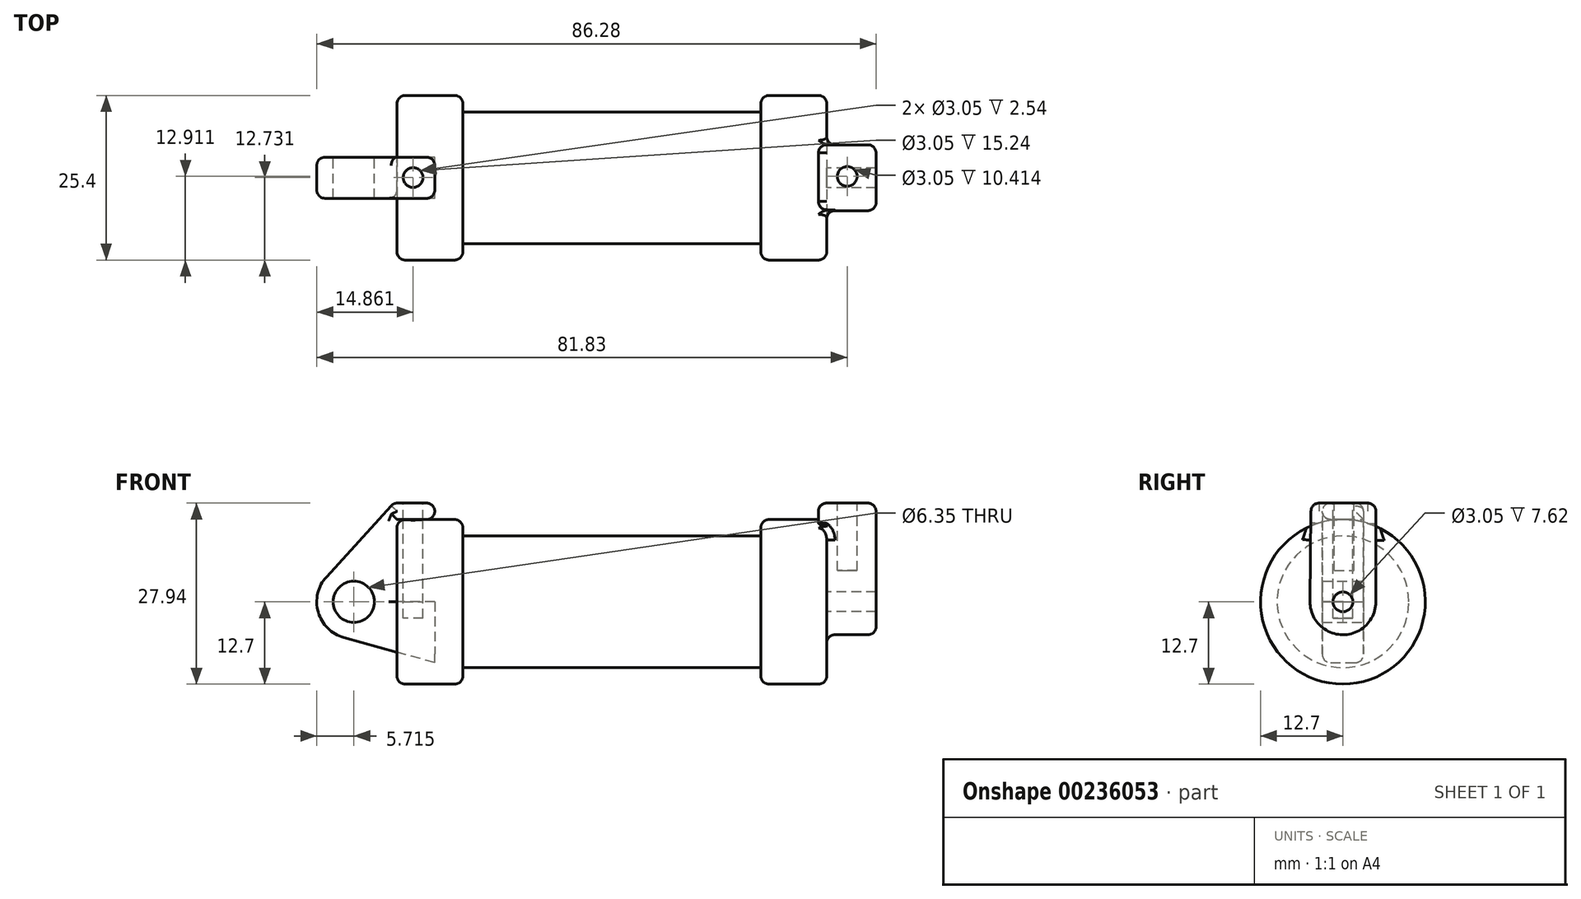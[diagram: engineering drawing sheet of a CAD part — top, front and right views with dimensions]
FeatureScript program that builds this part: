
annotation { "Feature Type Name" : "Feature", "Feature Type Description" : "" }
export const myFeature = defineFeature(function(context is Context, id is Id, definition is map)
    precondition{}
    {
        {
            var Q0;
            Q0=qCreatedBy(makeId("Front.planeOp"),FACE);
            var sketch = newSketch(context, id + "F0", { "sketchPlane" : qUnion([Q0])});
            skLineSegment(sketch, "E0", {"start": v(0, 0) * mm, "end": v(0, 12.7) * mm});
            skLineSegment(sketch, "E1", {"start": v(0, 12.7) * mm, "end": v(10.16, 12.7) * mm});
            skLineSegment(sketch, "E2", {"start": v(10.16, 12.7) * mm, "end": v(10.16, 10.16) * mm});
            skLineSegment(sketch, "E3", {"start": v(10.16, 10.16) * mm, "end": v(56.13, 10.16) * mm});
            skLineSegment(sketch, "E4", {"start": v(56.13, 10.16) * mm, "end": v(56.13, 12.7) * mm});
            skLineSegment(sketch, "E5", {"start": v(56.13, 12.7) * mm, "end": v(66.3, 12.7) * mm});
            skLineSegment(sketch, "E6", {"start": v(66.3, 12.7) * mm, "end": v(66.3, 0) * mm});
            skLineSegment(sketch, "E7", {"start": v(66.3, 0) * mm, "end": v(0, 0) * mm});
            skLineSegment(sketch, "E8", {"start": v(5.84, 15.24) * mm, "end": v(-0.5, 15.24) * mm});
            skLineSegment(sketch, "E9", {"start": v(-0.5, 15.24) * mm, "end": v(-10.88, 3.85) * mm});
            skLineSegment(sketch, "E10", {"start": v(0, 0) * mm, "end": v(-6.65, 0) * mm});
            skCircle(sketch, "E11", {"center": v(-6.65, 0) * mm, "radius": 5.72 * mm});
            skCircle(sketch, "E12", {"center": v(-6.65, 0) * mm, "radius": 3.18 * mm});
            skLineSegment(sketch, "E13", {"start": v(5.84, 15.24) * mm, "end": v(5.84, -9.4) * mm});
            skLineSegment(sketch, "E14", {"start": v(5.84, -9.4) * mm, "end": v(-8.18, -5.5) * mm});
            skSolve(sketch);
        }
        {
            var Q0;
            {var subQ0=sQuery(id+"F0.wireOp",EDGE,"E0");Q0=makeQuery(id+"F0.imprint","IMPRINT",FACE,{"disambiguationData":[TD([[makeQuery(id+"F0.imprint","IMPRINT",EDGE,{"derivedFrom":subQ0}),-1.0]])]});}
            var Q1;
            {var subQ0=sQuery(id+"F0.wireOp",EDGE,"E2");Q1=makeQuery(id+"F0.imprint","IMPRINT",FACE,{"disambiguationData":[TD([[makeQuery(id+"F0.imprint","IMPRINT",EDGE,{"derivedFrom":subQ0}),-1.0]])]});}
            var Q2;
            Q2=sQuery(id+"F0.wireOp",EDGE,"E7");
            revolve(context, id + "F1", {"entities" : qUnion([Q0, Q1]), "axis" : qUnion([Q2]), "revolveType" : RevolveType.FULL});
        }
        {
            var Q0;
            {var subQ3=sQuery(id+"F0.wireOp",EDGE,"E0");Q0=makeQuery(id+"F0.imprint","IMPRINT",FACE,{"disambiguationData":[TD([[makeQuery(id+"F0.imprint","IMPRINT",EDGE,{"derivedFrom":subQ3}),1.0]])]});}
            var Q1;
            {var subQ4=sQuery(id+"F0.wireOp",EDGE,"E12");Q1=makeQuery(id+"F0.imprint","IMPRINT",FACE,{"disambiguationData":[TD([[makeQuery(id+"F0.imprint","IMPRINT",EDGE,{"derivedFrom":subQ4}),-1.0]])]});}
            var Q2;
            {var subQ0=sQuery(id+"F0.wireOp",EDGE,"E14");Q2=makeQuery(id+"F0.imprint","IMPRINT",FACE,{"disambiguationData":[TD([[makeQuery(id+"F0.imprint","IMPRINT",EDGE,{"derivedFrom":subQ0}),-1.0]])]});}
            extrude(context, id + "F2", {"entities" : qUnion([Q0, Q1, Q2]), "endBound" : BoundingType.SYMMETRIC, "depth" : 6.35 * mm});
        }
        {
            var Q0;
            Q0=makeQuery(id+"F1.opRevolve","SWEPT_FACE",FACE,{"disambiguationData":[OSD([sQuery(id+"F0.wireOp",EDGE,"E6")])]});
            var sketch = newSketch(context, id + "F3", { "sketchPlane" : qUnion([Q0])});
            skCircle(sketch, "E15", {"center": v(0, 0) * mm, "radius": 5.08 * mm});
            skCircle(sketch, "E16", {"center": v(0, 0) * mm, "radius": 1.52 * mm});
            skLineSegment(sketch, "E17", {"start": v(5.08, 0) * mm, "end": v(5.09, 15.24) * mm});
            skLineSegment(sketch, "E18", {"start": v(5.09, 15.24) * mm, "end": v(-4.9, 15.24) * mm});
            skLineSegment(sketch, "E19", {"start": v(-4.9, 15.24) * mm, "end": v(-5.08, 0.03) * mm});
            skSolve(sketch);
        }
        {
            var Q0;
            Q0 = qSketchRegion(id + "F3", true);
            extrude(context, id + "F4", {"entities" : qUnion([Q0]), "operationType" : NewBodyOperationType.ADD, "depth" : 7.62 * mm, "hasSecondDirection" : true, "secondDirectionOppositeDirection" : true, "secondDirectionDepth" : 1.27 * mm});
        }
        {
            var Q0;
            Q0=makeQuery(id+"F4.boolean.opBoolean","SPLIT",FACE,{"disambiguationData":[TD([makeQuery(id+"F4.opExtrude","SWEPT_FACE",FACE,{"disambiguationData":[OSD([sQuery(id+"F3.wireOp",EDGE,"E16")])]})])],"derivedFrom":makeQuery(id+"F1.opRevolve","SWEPT_FACE",FACE,{"disambiguationData":[OSD([sQuery(id+"F0.wireOp",EDGE,"E6")])]})});
            extrude(context, id + "F5", {"entities" : qUnion([Q0]), "operationType" : NewBodyOperationType.REMOVE, "depth" : 56.13 * mm});
        }
        {
            var Q0;
            Q0=makeQuery(id+"F2.opExtrude","SWEPT_FACE",FACE,{"disambiguationData":[OSD([sQuery(id+"F0.wireOp",EDGE,"E8")])]});
            var sketch = newSketch(context, id + "F6", { "sketchPlane" : qUnion([Q0])});
            skCircle(sketch, "E20", {"center": v(2.5, 0.03) * mm, "radius": 1.52 * mm});
            skSolve(sketch);
        }
        {
            var Q0;
            Q0 = qSketchRegion(id + "F6", true);
            extrude(context, id + "F7", {"entities" : qUnion([Q0]), "operationType" : NewBodyOperationType.REMOVE, "oppositeDirection" : true, "depth" : 17.78 * mm});
        }
        {
            var Q0;
            Q0=makeQuery(id+"F4.opExtrude","SWEPT_FACE",FACE,{"disambiguationData":[OSD([sQuery(id+"F3.wireOp",EDGE,"E18")])]});
            var sketch = newSketch(context, id + "F8", { "sketchPlane" : qUnion([Q0])});
            skCircle(sketch, "E21", {"center": v(69.46, 0.2) * mm, "radius": 1.52 * mm});
            skSolve(sketch);
        }
        {
            var Q0;
            Q0 = qSketchRegion(id + "F8", true);
            extrude(context, id + "F9", {"entities" : qUnion([Q0]), "operationType" : NewBodyOperationType.REMOVE, "oppositeDirection" : true, "depth" : 10.4 * mm});
        }
        {
            var Q0;
            Q0=makeQuery(id+"F1.opRevolve","SWEPT_EDGE",EDGE,{"disambiguationData":[OSD([sQuery(id+"F0.wireOp",EDGE,"E1"),sQuery(id+"F0.wireOp",EDGE,"E2")])]});
            fillet(context, id + "F10", {"entities" : qUnion([Q0]), "radius" : 1.27 * mm, "tangentPropagation" : true, "allowEdgeOverflow" : false});
        }
        {
            var Q0;
            Q0=makeQuery(id+"F1.opRevolve","SWEPT_EDGE",EDGE,{"disambiguationData":[OSD([sQuery(id+"F0.wireOp",EDGE,"E4"),sQuery(id+"F0.wireOp",EDGE,"E5")])]});
            fillet(context, id + "F11", {"entities" : qUnion([Q0]), "radius" : 1.27 * mm, "tangentPropagation" : true, "allowEdgeOverflow" : false});
        }
        {
            var Q0;
            Q0=makeQuery(id+"F1.opRevolve","SWEPT_EDGE",EDGE,{"disambiguationData":[OSD([sQuery(id+"F0.wireOp",EDGE,"E5"),sQuery(id+"F0.wireOp",EDGE,"E6")])]});
            fillet(context, id + "F12", {"entities" : qUnion([Q0]), "radius" : 1.27 * mm, "tangentPropagation" : true, "allowEdgeOverflow" : false});
        }
        {
            var Q0;
            Q0=makeQuery(id+"F1.opRevolve","SWEPT_EDGE",EDGE,{"disambiguationData":[OSD([sQuery(id+"F0.wireOp",EDGE,"E0"),sQuery(id+"F0.wireOp",EDGE,"E1")])]});
            fillet(context, id + "F13", {"entities" : qUnion([Q0]), "radius" : 1.27 * mm, "tangentPropagation" : true, "allowEdgeOverflow" : false});
        }
        {
            var Q0;
            Q0=makeQuery(id+"F4.opExtrude","CAP_EDGE",EDGE,{"disambiguationData":[OSD([sQuery(id+"F3.wireOp",EDGE,"E18")])],"isStart":false});
            var Q1;
            Q1=makeQuery(id+"F4.opExtrude","CAP_EDGE",EDGE,{"disambiguationData":[OSD([sQuery(id+"F3.wireOp",EDGE,"E19")])],"isStart":false});
            var Q2;
            Q2=makeQuery(id+"F4.opExtrude","CAP_EDGE",EDGE,{"disambiguationData":[OSD([sQuery(id+"F3.wireOp",EDGE,"E15")])],"isStart":false});
            var Q3;
            Q3=makeQuery(id+"F4.opExtrude","SWEPT_EDGE",EDGE,{"disambiguationData":[OSD([sQuery(id+"F3.wireOp",EDGE,"E18"),sQuery(id+"F3.wireOp",EDGE,"E19")])]});
            var Q4;
            Q4=makeQuery(id+"F4.opExtrude","CAP_EDGE",EDGE,{"disambiguationData":[OSD([sQuery(id+"F3.wireOp",EDGE,"E18")])],"isStart":true});
            var Q5;
            Q5=makeQuery(id+"F4.opExtrude","SWEPT_EDGE",EDGE,{"disambiguationData":[OSD([sQuery(id+"F3.wireOp",EDGE,"E17"),sQuery(id+"F3.wireOp",EDGE,"E18")])]});
            var Q6;
            Q6=makeQuery(id+"F4.opExtrude","SWEPT_FACE",FACE,{"disambiguationData":[OSD([sQuery(id+"F3.wireOp",EDGE,"E15")])]});
            fillet(context, id + "F14", {"entities" : qUnion([Q0, Q1, Q2, Q3, Q4, Q5, Q6]), "radius" : 1.27 * mm, "tangentPropagation" : true, "allowEdgeOverflow" : false});
        }
        {
            var Q0;
            Q0=makeQuery(id+"F2.opExtrude","CAP_EDGE",EDGE,{"disambiguationData":[OSD([sQuery(id+"F0.wireOp",EDGE,"E8")])],"isStart":false});
            var Q1;
            Q1=makeQuery(id+"F2.opExtrude","CAP_EDGE",EDGE,{"disambiguationData":[OSD([sQuery(id+"F0.wireOp",EDGE,"E8")])],"isStart":true});
            var Q2;
            Q2=makeQuery(id+"F2.opExtrude","SWEPT_EDGE",EDGE,{"disambiguationData":[OSD([sQuery(id+"F0.wireOp",EDGE,"E8"),sQuery(id+"F0.wireOp",EDGE,"E9")])]});
            var Q3;
            Q3=makeQuery(id+"F2.opExtrude","SWEPT_EDGE",EDGE,{"disambiguationData":[OSD([sQuery(id+"F0.wireOp",EDGE,"E8"),sQuery(id+"F0.wireOp",EDGE,"E13")])]});
            var Q4;
            Q4=makeQuery(id+"F2.opExtrude","SWEPT_EDGE",EDGE,{"disambiguationData":[OSD([sQuery(id+"F0.wireOp",EDGE,"E1"),sQuery(id+"F0.wireOp",EDGE,"E13")])]});
            var Q5;
            {var subQ0=sQuery(id+"F0.wireOp",EDGE,"E13");Q5=makeQuery(id+"F2.opExtrude","CAP_EDGE",EDGE,{"disambiguationData":[OSD([subQ0]),TDD([makeQuery(id+"F0.imprint","IMPRINT",EDGE,{"disambiguationData":[TD([[makeQuery(id+"F0.imprint","INTERSECT",VERTEX,{"derivedFrom":[sQuery(id+"F0.wireOp",EDGE,"E8"),subQ0]}),-1.0]])],"derivedFrom":subQ0})])],"isStart":true});}
            var Q6;
            {var subQ0=sQuery(id+"F0.wireOp",EDGE,"E13");Q6=makeQuery(id+"F2.opExtrude","CAP_EDGE",EDGE,{"disambiguationData":[OSD([subQ0]),TDD([makeQuery(id+"F0.imprint","IMPRINT",EDGE,{"disambiguationData":[TD([[makeQuery(id+"F0.imprint","INTERSECT",VERTEX,{"derivedFrom":[sQuery(id+"F0.wireOp",EDGE,"E8"),subQ0]}),-1.0]])],"derivedFrom":subQ0})])],"isStart":false});}
            var Q7;
            Q7=makeQuery(id+"F2.opExtrude","CAP_EDGE",EDGE,{"disambiguationData":[OSD([sQuery(id+"F0.wireOp",EDGE,"E1")])],"isStart":false});
            var Q8;
            Q8=makeQuery(id+"F2.opExtrude","CAP_EDGE",EDGE,{"disambiguationData":[OSD([sQuery(id+"F0.wireOp",EDGE,"E0")])],"isStart":false});
            var Q9;
            Q9=makeQuery(id+"F2.opExtrude","CAP_EDGE",EDGE,{"disambiguationData":[OSD([sQuery(id+"F0.wireOp",EDGE,"E9")])],"isStart":false});
            var Q10;
            Q10=makeQuery(id+"F2.opExtrude","CAP_EDGE",EDGE,{"disambiguationData":[OSD([sQuery(id+"F0.wireOp",EDGE,"E11")])],"isStart":false});
            fillet(context, id + "F15", {"entities" : qUnion([Q0, Q1, Q2, Q3, Q4, Q5, Q6, Q7, Q8, Q9, Q10]), "radius" : 1.27 * mm, "tangentPropagation" : true, "allowEdgeOverflow" : false});
        }
        {
            var Q0;
            {var subQ0=sQuery(id+"F3.wireOp",EDGE,"E18");Q0=makeQuery(id+"F14.opFillet","BLEND_EDGE",EDGE,{"blendedFrom":[makeQuery(id+"F4.opExtrude","SWEPT_EDGE",EDGE,{"disambiguationData":[OSD([sQuery(id+"F3.wireOp",EDGE,"E17"),subQ0])]}),makeQuery(id+"F4.opExtrude","CAP_EDGE",EDGE,{"disambiguationData":[OSD([subQ0])],"isStart":true})],"blendedInto":[]});}
            var Q1;
            {var subQ0=sQuery(id+"F3.wireOp",EDGE,"E18");Q1=makeQuery(id+"F14.opFillet","BLEND_EDGE",EDGE,{"blendedFrom":[makeQuery(id+"F4.opExtrude","SWEPT_EDGE",EDGE,{"disambiguationData":[OSD([subQ0,sQuery(id+"F3.wireOp",EDGE,"E19")])]}),makeQuery(id+"F4.opExtrude","CAP_EDGE",EDGE,{"disambiguationData":[OSD([subQ0])],"isStart":true})],"blendedInto":[]});}
            var Q2;
            {var subQ0=sQuery(id+"F0.wireOp",EDGE,"E8");Q2=makeQuery(id+"F15.opFillet","BLEND_EDGE",EDGE,{"blendedFrom":[makeQuery(id+"F2.opExtrude","SWEPT_EDGE",EDGE,{"disambiguationData":[OSD([subQ0,sQuery(id+"F0.wireOp",EDGE,"E9")])]}),makeQuery(id+"F2.opExtrude","CAP_EDGE",EDGE,{"disambiguationData":[OSD([subQ0])],"isStart":true})],"blendedInto":[]});}
            fillet(context, id + "F16", {"entities" : qUnion([Q0, Q1, Q2]), "radius" : 1.27 * mm, "tangentPropagation" : true, "allowEdgeOverflow" : false});
        }
    });
